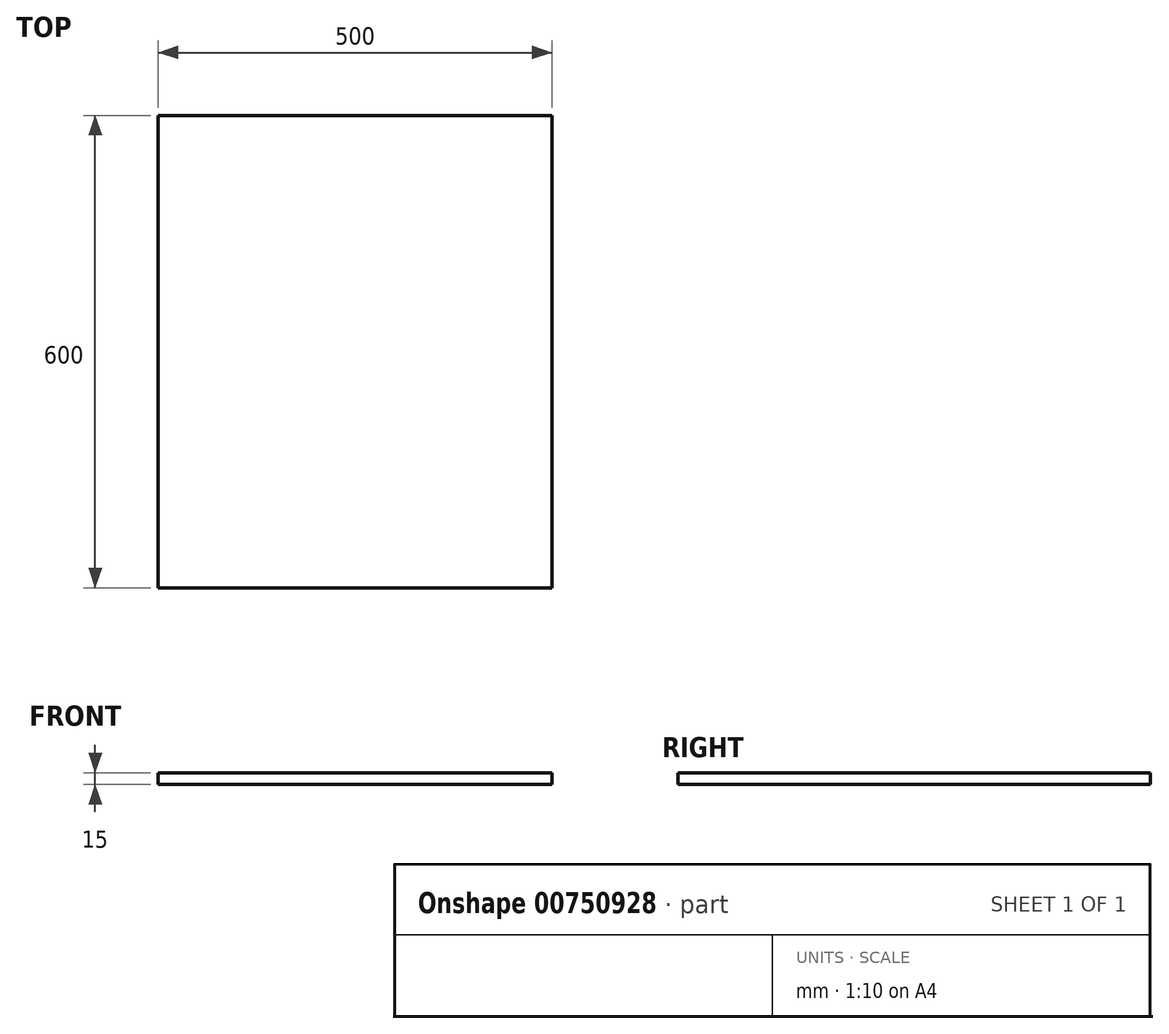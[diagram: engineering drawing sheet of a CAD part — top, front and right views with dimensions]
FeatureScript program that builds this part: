
annotation { "Feature Type Name" : "Feature", "Feature Type Description" : "" }
export const myFeature = defineFeature(function(context is Context, id is Id, definition is map)
    precondition{}
    {
        {
            var Q0;
            Q0=qCreatedBy(makeId("Top.planeOp"),FACE);
            var sketch = newSketch(context, id + "F0", { "sketchPlane" : qUnion([Q0])});
            skLineSegment(sketch, "E0.bottom", {"start": v(250, -300) * mm, "end": v(-250, -300) * mm});
            skLineSegment(sketch, "E0.top", {"start": v(250, 300) * mm, "end": v(-250, 300) * mm});
            skLineSegment(sketch, "E0.left", {"start": v(250, -300) * mm, "end": v(250, 300) * mm});
            skLineSegment(sketch, "E0.right", {"start": v(-250, -300) * mm, "end": v(-250, 300) * mm});
            skPoint(sketch, "E0.middle", {"position": v(0, 0) * mm});
            skSolve(sketch);
        }
        {
            var Q0;
            Q0 = qSketchRegion(id + "F0", true);
            extrude(context, id + "F1", {"entities" : qUnion([Q0]), "depth" : 15 * mm, "offsetDistance" : 25 * mm});
        }
    });
